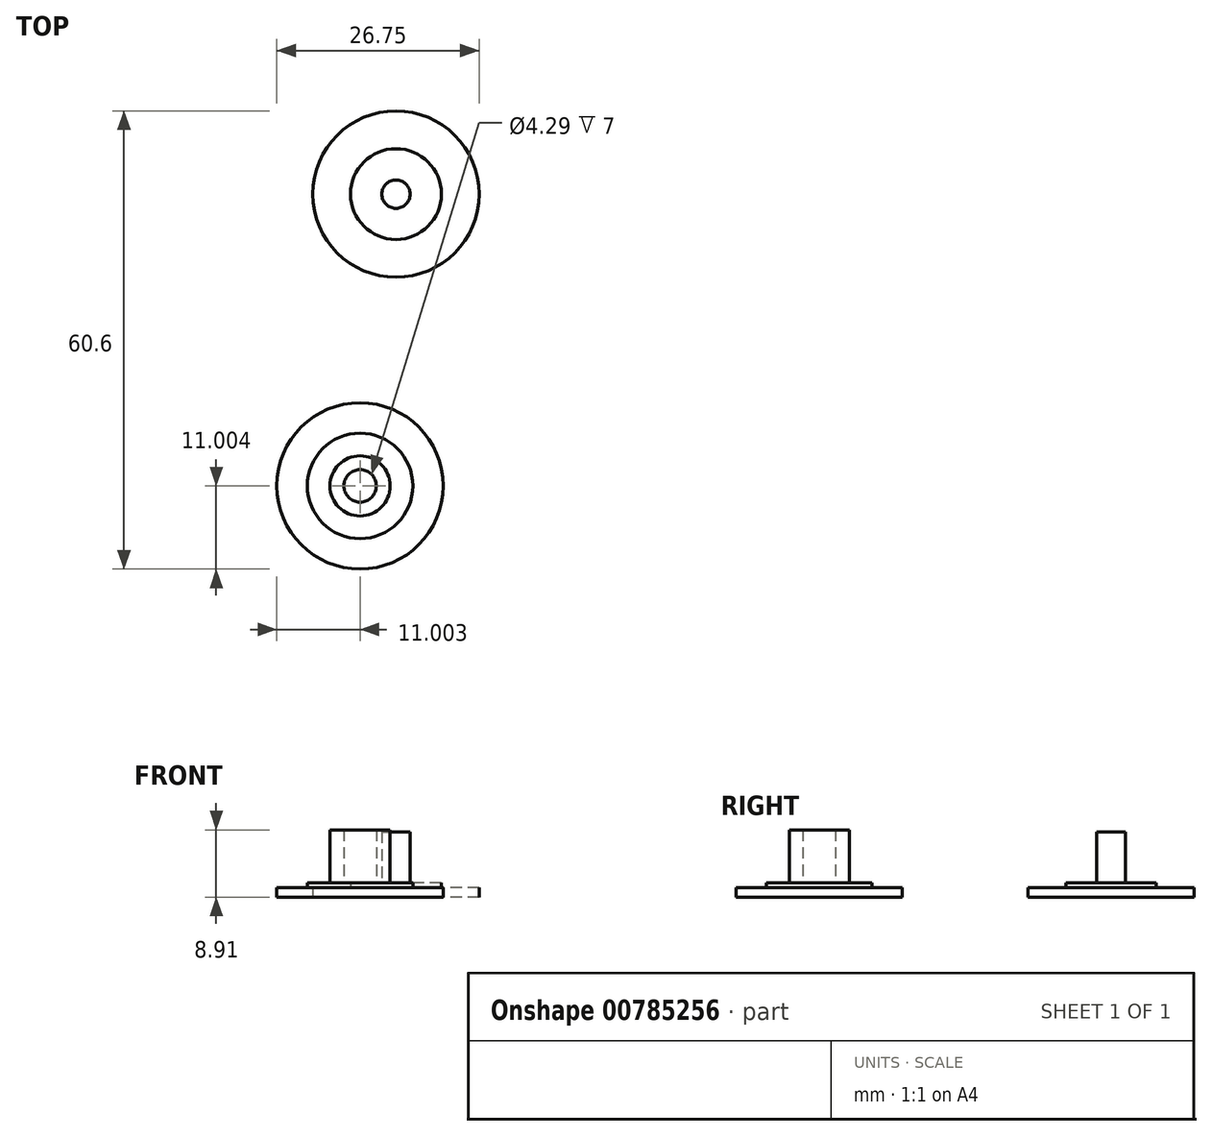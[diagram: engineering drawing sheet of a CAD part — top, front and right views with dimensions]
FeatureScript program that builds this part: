
annotation { "Feature Type Name" : "Feature", "Feature Type Description" : "" }
export const myFeature = defineFeature(function(context is Context, id is Id, definition is map)
    precondition{}
    {
        {
            var Q0;
            Q0=qCreatedBy(makeId("Top.planeOp"),FACE);
            var sketch = newSketch(context, id + "F0", { "sketchPlane" : qUnion([Q0])});
            skCircle(sketch, "E0", {"center": v(0, 0) * mm, "radius": 11.25 * mm});
            skCircle(sketch, "E1", {"center": v(-22.62, -15.64) * mm, "radius": 11.25 * mm});
            skCircle(sketch, "E2", {"center": v(24.85, -11.77) * mm, "radius": 11.25 * mm});
            skCircle(sketch, "E3", {"center": v(-2.23, 27.4) * mm, "radius": 11.25 * mm});
            skCircle(sketch, "E4.0", {"center": v(-22.62, -15.64) * mm, "radius": 15.25 * mm});
            skCircle(sketch, "E5.0", {"center": v(-2.23, 27.4) * mm, "radius": 15.25 * mm});
            skCircle(sketch, "E6.0", {"center": v(24.85, -11.77) * mm, "radius": 15.25 * mm});
            skLineSegment(sketch, "E7", {"start": v(-16.1, -1.86) * mm, "end": v(-8.76, 13.63) * mm, "construction": true});
            skLineSegment(sketch, "E8", {"start": v(16.18, 0.77) * mm, "end": v(6.44, 14.87) * mm, "construction": true});
            skLineSegment(sketch, "E9", {"start": v(-7.42, -14.4) * mm, "end": v(9.65, -13) * mm, "construction": true});
            skArc(sketch, "E10", {"start": v(11.8, -19.65) * mm, "mid": v(1.16, -14.2) * mm, "end": v(-8.46, -21.3) * mm});
            skArc(sketch, "E11", {"start": v(-22.92, -0.4) * mm, "mid": v(-12.88, 6.1) * mm, "end": v(-14.22, 17.98) * mm});
            skArc(sketch, "E12", {"start": v(11.12, 20.04) * mm, "mid": v(11.72, 8.1) * mm, "end": v(22.68, 3.32) * mm});
            skSolve(sketch);
        }
        {
            var Q0;
            Q0=makeQuery(id+"F0.imprint","IMPRINT",FACE,{"disambiguationData":[TD([[makeQuery(id+"F0.imprint","IMPRINT",EDGE,{"derivedFrom":sQuery(id+"F0.wireOp",EDGE,"E1")}),-1.0]])]});
            var Q1;
            Q1=makeQuery(id+"F0.imprint","IMPRINT",FACE,{"disambiguationData":[TD([[makeQuery(id+"F0.imprint","IMPRINT",EDGE,{"derivedFrom":sQuery(id+"F0.wireOp",EDGE,"E0")}),-1.0]])]});
            var Q2;
            Q2=makeQuery(id+"F0.imprint","IMPRINT",FACE,{"disambiguationData":[TD([[makeQuery(id+"F0.imprint","IMPRINT",EDGE,{"derivedFrom":sQuery(id+"F0.wireOp",EDGE,"E3")}),-1.0]])]});
            var Q3;
            Q3=makeQuery(id+"F0.imprint","IMPRINT",FACE,{"disambiguationData":[TD([[makeQuery(id+"F0.imprint","IMPRINT",EDGE,{"derivedFrom":sQuery(id+"F0.wireOp",EDGE,"E2")}),-1.0]])]});
            extrude(context, id + "F1", {"entities" : qUnion([Q0, Q1, Q2, Q3]), "depth" : 7 * mm, "offsetDistance" : 25.4 * mm});
        }
        {
            var Q0;
            Q0=makeQuery(id+"F1.opExtrude","CAP_EDGE",EDGE,{"disambiguationData":[OSD([sQuery(id+"F0.wireOp",EDGE,"E4.0")])],"isStart":false});
            fillet(context, id + "F2", {"entities" : qUnion([Q0]), "radius" : 2.3 * mm, "tangentPropagation" : true, "allowEdgeOverflow" : false});
        }
        {
            var Q0;
            Q0=makeQuery(id+"F1.opExtrude","CAP_EDGE",EDGE,{"disambiguationData":[OSD([sQuery(id+"F0.wireOp",EDGE,"E5.0")])],"isStart":true});
            fillet(context, id + "F3", {"entities" : qUnion([Q0]), "radius" : 2.3 * mm, "tangentPropagation" : true, "allowEdgeOverflow" : false});
        }
        {
            var Q0;
            Q0=qCreatedBy(makeId("Top.planeOp"),FACE);
            var sketch = newSketch(context, id + "F4", { "sketchPlane" : qUnion([Q0])});
            skCircle(sketch, "E13", {"center": v(-45.62, 18.56) * mm, "radius": 11 * mm});
            skCircle(sketch, "E14.0", {"center": v(-45.62, 18.56) * mm, "radius": 3.98 * mm});
            skCircle(sketch, "E15.0", {"center": v(-45.62, 18.56) * mm, "radius": 6.98 * mm});
            skCircle(sketch, "E16", {"center": v(-45.62, 18.56) * mm, "radius": 2.15 * mm});
            skSolve(sketch);
        }
        {
            var Q0;
            Q0=makeQuery(id+"F4.imprint","IMPRINT",FACE,{"disambiguationData":[TD([[makeQuery(id+"F4.imprint","IMPRINT",EDGE,{"derivedFrom":sQuery(id+"F4.wireOp",EDGE,"E13")}),1.0]])]});
            extrude(context, id + "F5", {"entities" : qUnion([Q0]), "depth" : 1.27 * mm, "offsetDistance" : 25.4 * mm});
        }
        {
            var Q0;
            Q0=makeQuery(id+"F4.imprint","IMPRINT",FACE,{"disambiguationData":[TD([[makeQuery(id+"F4.imprint","IMPRINT",EDGE,{"derivedFrom":sQuery(id+"F4.wireOp",EDGE,"E14.0")}),-1.0]])]});
            var Q1;
            Q1=makeQuery(id+"F4.imprint","IMPRINT",FACE,{"disambiguationData":[TD([[makeQuery(id+"F4.imprint","IMPRINT",EDGE,{"derivedFrom":sQuery(id+"F4.wireOp",EDGE,"E16")}),1.0]])]});
            extrude(context, id + "F6", {"entities" : qUnion([Q0, Q1]), "operationType" : NewBodyOperationType.ADD, "depth" : 1.9 * mm, "offsetDistance" : 25.4 * mm});
        }
        {
            var Q0;
            Q0=makeQuery(id+"F4.imprint","IMPRINT",FACE,{"disambiguationData":[TD([[makeQuery(id+"F4.imprint","IMPRINT",EDGE,{"derivedFrom":sQuery(id+"F4.wireOp",EDGE,"E14.0")}),1.0]])]});
            extrude(context, id + "F7", {"entities" : qUnion([Q0]), "operationType" : NewBodyOperationType.ADD, "depth" : 8.9 * mm, "offsetDistance" : 25.4 * mm});
        }
        {
            var Q0;
            Q0=qCreatedBy(makeId("Top.planeOp"),FACE);
            var sketch = newSketch(context, id + "F8", { "sketchPlane" : qUnion([Q0])});
            skCircle(sketch, "E17", {"center": v(-40.87, 57.16) * mm, "radius": 11 * mm});
            skCircle(sketch, "E18", {"center": v(-40.87, 57.16) * mm, "radius": 6 * mm});
            skCircle(sketch, "E19", {"center": v(-40.87, 57.16) * mm, "radius": 1.88 * mm});
            skSolve(sketch);
        }
        {
            var Q0;
            Q0=makeQuery(id+"F8.imprint","IMPRINT",FACE,{"disambiguationData":[TD([[makeQuery(id+"F8.imprint","IMPRINT",EDGE,{"derivedFrom":sQuery(id+"F8.wireOp",EDGE,"E17")}),1.0]])]});
            extrude(context, id + "F9", {"entities" : qUnion([Q0]), "depth" : 1.27 * mm, "offsetDistance" : 25.4 * mm});
        }
        {
            var Q0;
            Q0=makeQuery(id+"F8.imprint","IMPRINT",FACE,{"disambiguationData":[TD([[makeQuery(id+"F8.imprint","IMPRINT",EDGE,{"derivedFrom":sQuery(id+"F8.wireOp",EDGE,"E18")}),1.0]])]});
            extrude(context, id + "F10", {"entities" : qUnion([Q0]), "operationType" : NewBodyOperationType.ADD, "depth" : 1.9 * mm, "offsetDistance" : 25.4 * mm});
        }
        {
            var Q0;
            Q0=makeQuery(id+"F8.imprint","IMPRINT",FACE,{"disambiguationData":[TD([[makeQuery(id+"F8.imprint","IMPRINT",EDGE,{"derivedFrom":sQuery(id+"F8.wireOp",EDGE,"E19")}),1.0]])]});
            extrude(context, id + "F11", {"entities" : qUnion([Q0]), "operationType" : NewBodyOperationType.ADD, "depth" : 8.65 * mm, "offsetDistance" : 25.4 * mm});
        }
        {
            var Q0;
            Q0=makeQuery(id+"F1.opExtrude","SWEPT_BODY",BODY,{"disambiguationData":[OSD([sQuery(id+"F0.wireOp",EDGE,"E0"),sQuery(id+"F0.wireOp",EDGE,"E1"),sQuery(id+"F0.wireOp",EDGE,"E2"),sQuery(id+"F0.wireOp",EDGE,"E3"),sQuery(id+"F0.wireOp",EDGE,"E4.0"),sQuery(id+"F0.wireOp",EDGE,"E5.0"),sQuery(id+"F0.wireOp",EDGE,"E6.0"),sQuery(id+"F0.wireOp",EDGE,"E10"),sQuery(id+"F0.wireOp",EDGE,"E11"),sQuery(id+"F0.wireOp",EDGE,"E12")])]});
            deleteBodies(context, id + "F12", {"entities" : qUnion([Q0])});
        }
    });
